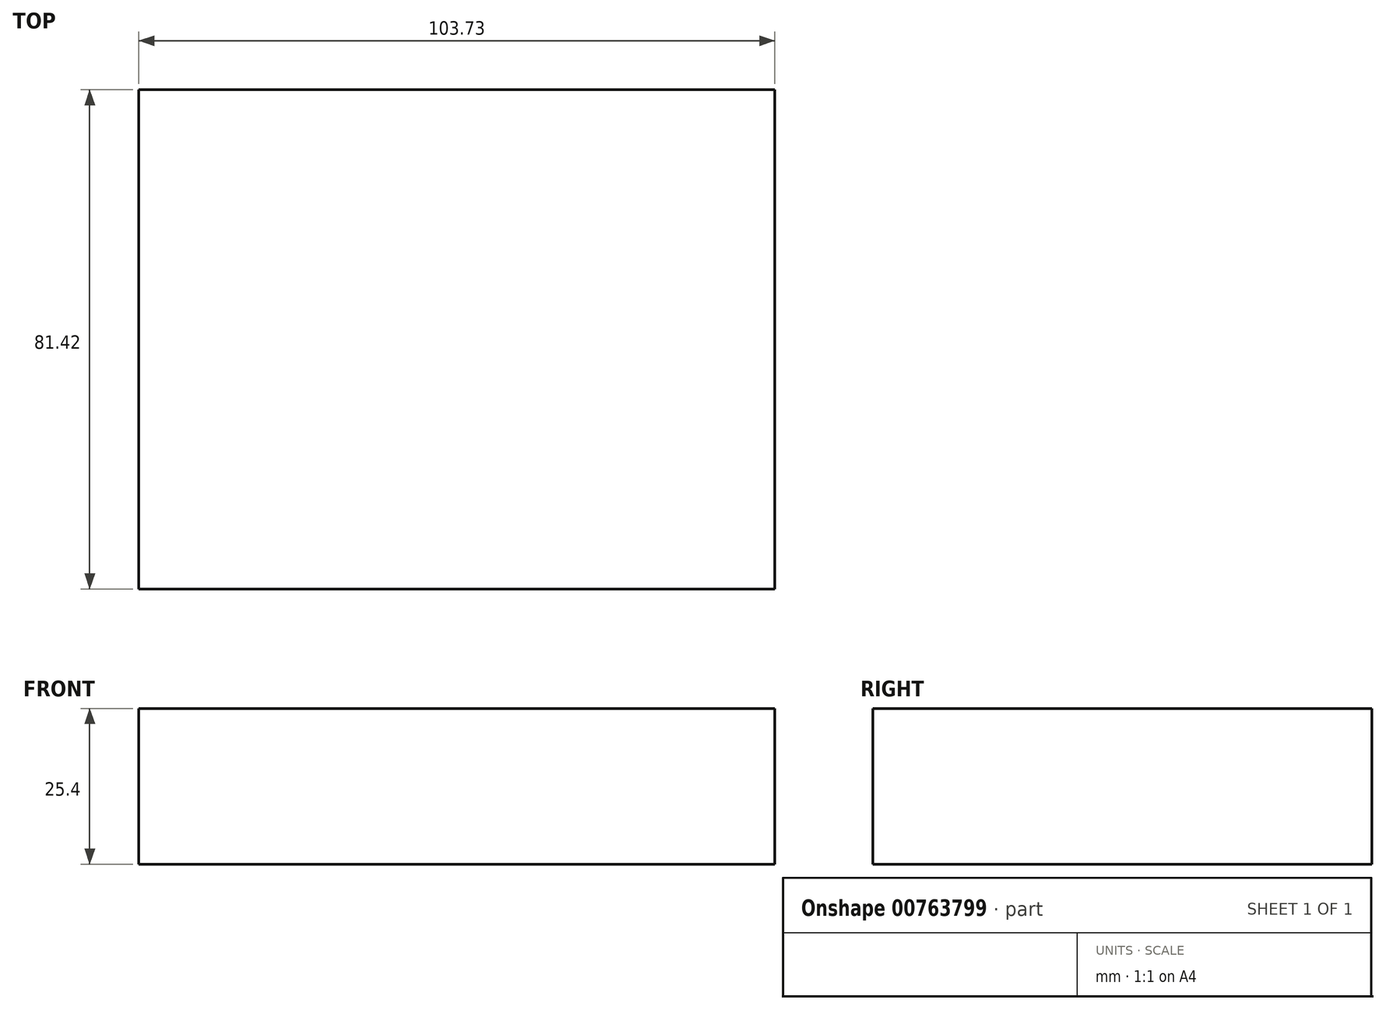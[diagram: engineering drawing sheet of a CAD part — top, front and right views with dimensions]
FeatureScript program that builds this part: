
annotation { "Feature Type Name" : "Feature", "Feature Type Description" : "" }
export const myFeature = defineFeature(function(context is Context, id is Id, definition is map)
    precondition{}
    {
        {
            var Q0;
            Q0=qCreatedBy(makeId("Top.planeOp"),FACE);
            var sketch = newSketch(context, id + "F0", { "sketchPlane" : qUnion([Q0])});
            skLineSegment(sketch, "E0.bottom", {"start": v(-45.07, 35.13) * mm, "end": v(58.66, 35.13) * mm});
            skLineSegment(sketch, "E0.top", {"start": v(-45.07, -46.29) * mm, "end": v(58.66, -46.29) * mm});
            skLineSegment(sketch, "E0.left", {"start": v(-45.07, 35.13) * mm, "end": v(-45.07, -46.29) * mm});
            skLineSegment(sketch, "E0.right", {"start": v(58.66, 35.13) * mm, "end": v(58.66, -46.29) * mm});
            skSolve(sketch);
        }
        {
            var Q0;
            Q0=makeQuery(id+"F0.imprint","IMPRINT",FACE,{"disambiguationData":[TD([[makeQuery(id+"F0.imprint","IMPRINT",EDGE,{"derivedFrom":sQuery(id+"F0.wireOp",EDGE,"E0.bottom")}),-1.0]])]});
            extrude(context, id + "F1", {"entities" : qUnion([Q0]), "depth" : 25.4 * mm, "offsetDistance" : 25.4 * mm});
        }
    });
